# Revit family: equip-water-cooler-hlsy-tylr-hthb-hrfsebp-i
name_source: partatom
category: Plumbing Fixtures
units: mm (PartAtom-declared; Revit-internal decimal feet)

## family parameters
Always vertical = Yes
Cut with Voids When Loaded = No
OmniClass Number = 23.45.00.00
OmniClass Title = Sanitary, Laundry, and Cleaning Equipment
Part Type = Normal
Room Calculation Point = No
Round Connector Dimension = Use Radius
Shared = No
Work Plane-Based = No

## types (1)
- equip-water-cooler-hlsy-tylr-hthb-hrfsebp-i
    Activation = Sensor
    Apparent Load Phase 1 = 0 VA
    Basin Material = Metal - Steel - Stainless - Chrome
    Body Material = Metal - Steel - Stainless - Chrome
    Bottle Apparent Load Phase 1 = 0 VA
    Bottle Number of Poles = 1
    Bottle Power Factor = 0
    Bottle Voltage = 0 V
    Bottle Water Service Flow = 0 GPM
    Bottle Water Service Flow Out = 0 GPM
    Bottle Water Service Size Radius = 0' - 0 5/8"
    Bubbler = Double Bubbler
    Bubbler Material = Metal - Steel - Stainless - Chrome
    Button Material = Metal - Steel - Stainless - Chrome
    CW Connection = Yes
    Chiller = NONE
    Chiller Option = No
    Cooler Depth = 1' - 6"
    Cooler Width = 5' - 0 1/8"
    Description = Water Cooler
    Filter = NONE
    Fountain = HRFSEBPWSI_NF
    HW Connection = No
    Lower Unit Rim Height = 2' - 10"
    Manufacturer = Halsey Taylor
    Model = HTHB-HRFSEBP-1
    Mounting = MFWS200
    Number of Poles = 1
    Plastic One Material = Metal - Steel - Stainless - Color 3
    Plastic Two Material = Metal - Steel - Stainless - Aztec Gold
    Power Factor = 0
    Sanitary Connector Description = Sanitary Connection
    Sanitary Service Size Radius = 0' - 0 5/8"
    Type = Single
    URL = http://halseytaylor.com
    Upper Unit Rim Height = 3' - 4"
    Vent Connection = No
    Version = 1.0.0.0
    Voltage = 0 V
    Volts/Hertz = 115V/60Hz
    Wall Plate Material = Metal - Steel - Stainless - Chrome
    Waste Connection = Yes
    Water Connector Description = Water Supply
    Water Out Connection Description = Water Return
    Water Service Flow = 0 GPM
    Water Service Flow Out = 0 GPM
    Water Service Size Radius = 0' - 0 1/4"

## geometry (parser evidence)
native form markers: Sweep x6
no freeform markers — native parametric forms only
